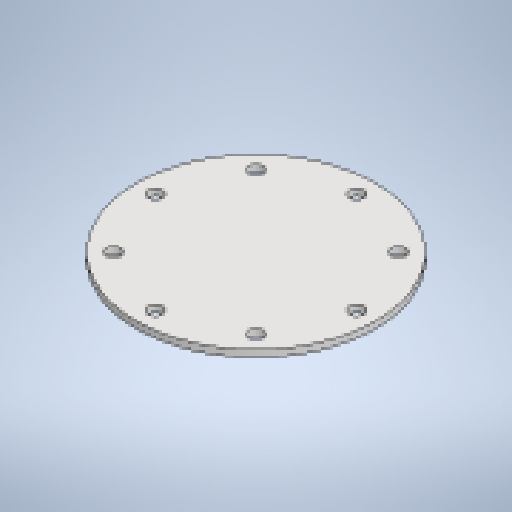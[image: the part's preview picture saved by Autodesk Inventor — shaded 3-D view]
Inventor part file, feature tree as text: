
AUTODESK INVENTOR PART (.ipt)
format: ipt  version: 2025.1 (Build 291241020, 241B)  size: 193,536 bytes
history: native  units: mm
features: other x3, sketch x2, sheet_metal_op x1, pattern_circular x1
ambient origin geometry x8: Origin, YZ Plane, XZ Plane, XY Plane, X Axis, Y Axis, Z Axis, Center Point
bodies: Body1 (feature_tree)
feature tree (7):
  sheet_metal_op  "Face2"
  pattern_circular  "Circular Pattern1"  [2 undecoded]
  sketch  "Sketch2"  dims[d14=8.0mm]
  other  "Plate2"
  sketch  "Sketch3"  dims[d15=17.0mm d17=8.0mm d18=0.0mm d19=80.0mm d20=360.0deg d25=161.0mm d27=285.0mm d28=240.0mm]
  other  "Cut1"
  other  "Definition1"
note: 2 required parameter values undecoded (feature->parameter linkage not recoverable at this tier; creation-order binding heuristic only, values carry confidence <= 0.55)
